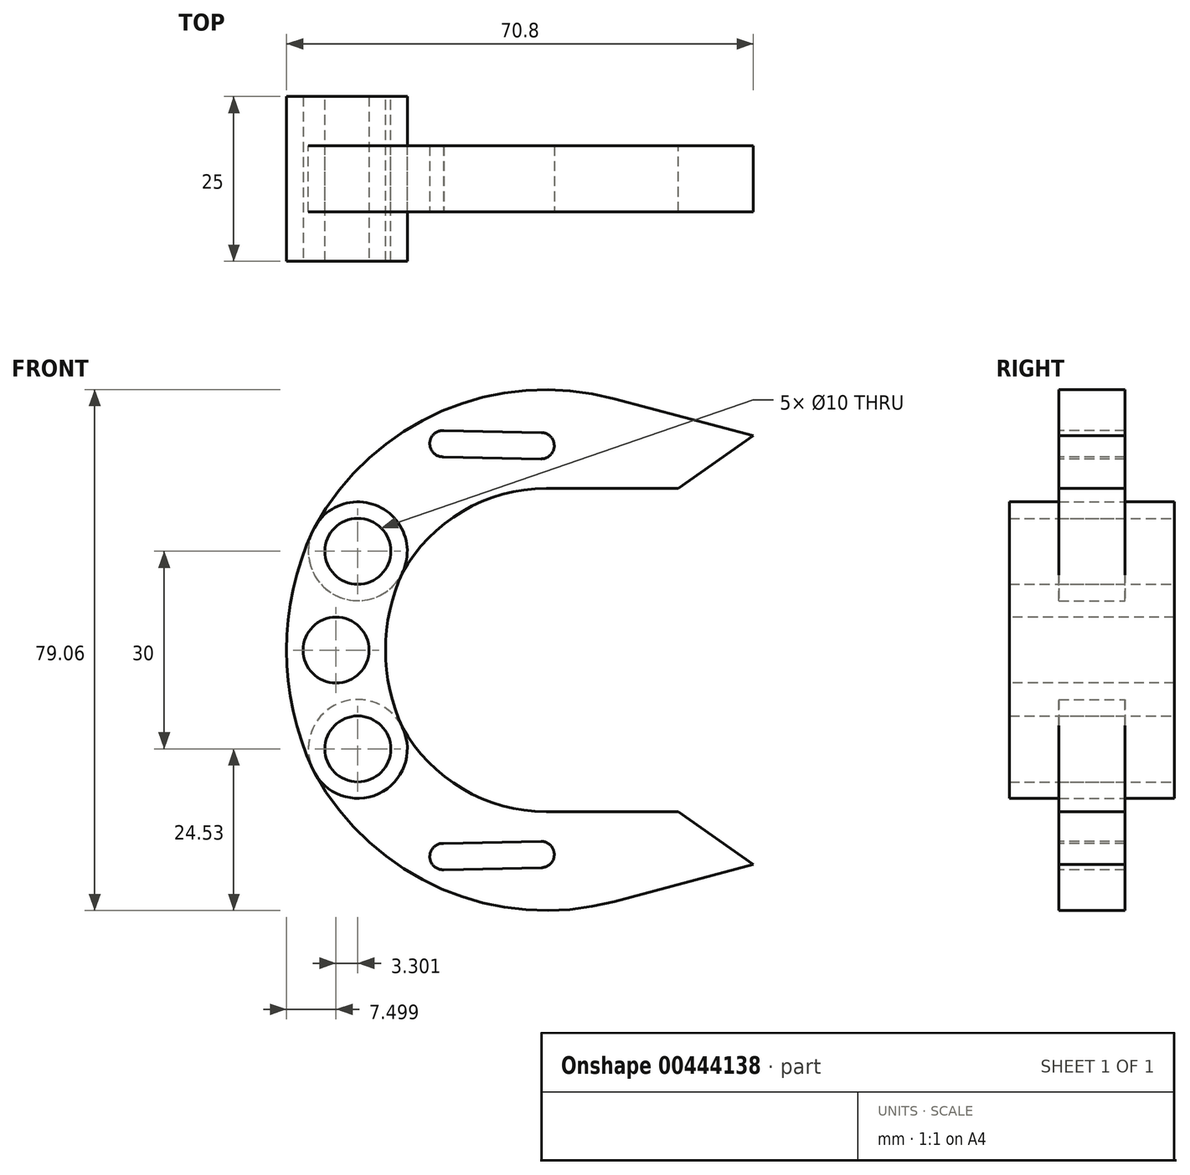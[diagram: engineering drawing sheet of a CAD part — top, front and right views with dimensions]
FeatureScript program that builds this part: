
annotation { "Feature Type Name" : "Feature", "Feature Type Description" : "" }
export const myFeature = defineFeature(function(context is Context, id is Id, definition is map)
    precondition{}
    {
        {
            var Q0;
            Q0=qCreatedBy(makeId("Front.planeOp"),FACE);
            var sketch = newSketch(context, id + "F0", { "sketchPlane" : qUnion([Q0])});
            skLineSegment(sketch, "E0", {"start": v(0, 15) * mm, "end": v(0, -15) * mm, "construction": true});
            skLineSegment(sketch, "E1", {"start": v(0, 0) * mm, "end": v(80, 0) * mm, "construction": true});
            skCircle(sketch, "E2", {"center": v(0, 15) * mm, "radius": 5 * mm});
            skCircle(sketch, "E3", {"center": v(0, -15) * mm, "radius": 5 * mm});
            skArc(sketch, "E4.0", {"start": v(6.8, 11.85) * mm, "mid": v(3.15, 21.8) * mm, "end": v(-6.8, 18.15) * mm});
            skArc(sketch, "E5.0", {"start": v(-6.8, -18.15) * mm, "mid": v(3.15, -21.8) * mm, "end": v(6.8, -11.85) * mm});
            skArc(sketch, "E6", {"start": v(-6.8, 18.15) * mm, "mid": v(-10.8, 0) * mm, "end": v(-6.8, -18.15) * mm});
            skArc(sketch, "E7", {"start": v(6.8, 11.85) * mm, "mid": v(4.2, 0) * mm, "end": v(6.8, -11.85) * mm});
            skPoint(sketch, "E8.orphan", {"position": v(0, -28.59) * mm});
            skSolve(sketch);
        }
        {
            var Q0;
            Q0=qCreatedBy(makeId("Front.planeOp"),FACE);
            var sketch = newSketch(context, id + "F1", { "sketchPlane" : qUnion([Q0])});
            skCircle(sketch, "E9.0", {"center": v(0, 15) * mm, "radius": 5 * mm});
            skCircle(sketch, "E10", {"center": v(0, 15) * mm, "radius": 7.5 * mm});
            skArc(sketch, "E11", {"start": v(38.92, 38.17) * mm, "mid": v(12.76, 36.27) * mm, "end": v(-6.6, 18.57) * mm});
            skLineSegment(sketch, "E12", {"start": v(38.92, 38.17) * mm, "end": v(60, 32.53) * mm});
            skLineSegment(sketch, "E13", {"start": v(60, 32.53) * mm, "end": v(48.58, 24.53) * mm});
            skLineSegment(sketch, "E14", {"start": v(48.58, 24.53) * mm, "end": v(28.58, 24.53) * mm});
            skArc(sketch, "E15", {"start": v(28.58, 24.53) * mm, "mid": v(15.79, 21) * mm, "end": v(6.6, 11.43) * mm});
            skLineSegment(sketch, "E16", {"start": v(38.92, 38.17) * mm, "end": v(37.45, 29.8) * mm, "construction": true});
            skLineSegment(sketch, "E17", {"start": v(37.45, 29.8) * mm, "end": v(22.96, 33.68) * mm, "construction": true});
            skArc(sketch, "E18.MirrorCS", {"start": v(38.92, -38.17) * mm, "mid": v(12.76, -36.27) * mm, "end": v(-6.6, -18.57) * mm});
            skLineSegment(sketch, "E19.MirrorCS", {"start": v(38.92, -38.17) * mm, "end": v(60, -32.53) * mm});
            skLineSegment(sketch, "E20.MirrorCS", {"start": v(48.58, -24.53) * mm, "end": v(28.58, -24.53) * mm});
            skLineSegment(sketch, "E21.MirrorCS", {"start": v(60, -32.53) * mm, "end": v(48.58, -24.53) * mm});
            skArc(sketch, "E22.MirrorCS", {"start": v(28.58, -24.53) * mm, "mid": v(15.79, -21) * mm, "end": v(6.6, -11.43) * mm});
            skCircle(sketch, "E23.MirrorC", {"center": v(0, -15) * mm, "radius": 7.5 * mm});
            skCircle(sketch, "E24.MirrorC", {"center": v(0, -15) * mm, "radius": 5 * mm});
            skSolve(sketch);
        }
        {
            var Q0;
            Q0 = qSketchRegion(id + "F0", true);
            extrude(context, id + "F2", {"entities" : qUnion([Q0]), "endBound" : BoundingType.SYMMETRIC, "depth" : 25 * mm});
        }
        {
            var Q0;
            Q0 = qSketchRegion(id + "F1", true);
            extrude(context, id + "F3", {"entities" : qUnion([Q0]), "endBound" : BoundingType.SYMMETRIC, "depth" : 10 * mm});
        }
        {
            var Q0;
            Q0=makeQuery(id+"F3.opExtrude","CAP_FACE",FACE,{"disambiguationData":[OSD([sQuery(id+"F1.wireOp",EDGE,"E9.0"),sQuery(id+"F1.wireOp",EDGE,"E10"),sQuery(id+"F1.wireOp",EDGE,"E11"),sQuery(id+"F1.wireOp",EDGE,"E12"),sQuery(id+"F1.wireOp",EDGE,"E13"),sQuery(id+"F1.wireOp",EDGE,"E14"),sQuery(id+"F1.wireOp",EDGE,"E15")])],"isStart":false});
            var sketch = newSketch(context, id + "F4", { "sketchPlane" : qUnion([Q0])});
            skCircle(sketch, "E25", {"center": v(12.91, 31.34) * mm, "radius": 2 * mm});
            skCircle(sketch, "E26", {"center": v(27.8, 31.03) * mm, "radius": 2 * mm});
            skLineSegment(sketch, "E27", {"start": v(12.84, 33.33) * mm, "end": v(27.84, 33.03) * mm});
            skLineSegment(sketch, "E28", {"start": v(12.76, 29.34) * mm, "end": v(27.75, 29.03) * mm});
            skLineSegment(sketch, "E29", {"start": v(12.91, 31.34) * mm, "end": v(27.8, 31.03) * mm, "construction": true});
            skLineSegment(sketch, "E30", {"start": v(27.23, 39.5) * mm, "end": v(27.8, 31.03) * mm, "construction": true});
            skCircle(sketch, "E31.MirrorC", {"center": v(12.91, -31.34) * mm, "radius": 2 * mm});
            skCircle(sketch, "E32.MirrorC", {"center": v(27.8, -31.03) * mm, "radius": 2 * mm});
            skLineSegment(sketch, "E33.MirrorCS", {"start": v(12.76, -29.34) * mm, "end": v(27.75, -29.03) * mm});
            skLineSegment(sketch, "E34.MirrorCS", {"start": v(12.91, -31.34) * mm, "end": v(27.8, -31.03) * mm, "construction": true});
            skLineSegment(sketch, "E35.MirrorCS", {"start": v(27.23, -39.5) * mm, "end": v(27.8, -31.03) * mm, "construction": true});
            skLineSegment(sketch, "E36.MirrorCS", {"start": v(12.84, -33.33) * mm, "end": v(27.84, -33.03) * mm});
            skSolve(sketch);
        }
        {
            var Q0;
            Q0 = qSketchRegion(id + "F4", true);
            extrude(context, id + "F5", {"entities" : qUnion([Q0]), "operationType" : NewBodyOperationType.REMOVE, "endBound" : BoundingType.THROUGH_ALL, "oppositeDirection" : true, "depth" : 25 * mm});
        }
        {
            var Q0;
            Q0=makeQuery(id+"F2.opExtrude","CAP_FACE",FACE,{"disambiguationData":[OSD([sQuery(id+"F0.wireOp",EDGE,"E2"),sQuery(id+"F0.wireOp",EDGE,"E3"),sQuery(id+"F0.wireOp",EDGE,"E4.0"),sQuery(id+"F0.wireOp",EDGE,"E5.0"),sQuery(id+"F0.wireOp",EDGE,"E6"),sQuery(id+"F0.wireOp",EDGE,"E7")])],"isStart":false});
            var sketch = newSketch(context, id + "F6", { "sketchPlane" : qUnion([Q0])});
            skCircle(sketch, "E37", {"center": v(-3.3, 0) * mm, "radius": 5 * mm});
            skSolve(sketch);
        }
        {
            var Q0;
            Q0 = qSketchRegion(id + "F6", true);
            extrude(context, id + "F7", {"entities" : qUnion([Q0]), "operationType" : NewBodyOperationType.REMOVE, "endBound" : BoundingType.THROUGH_ALL, "oppositeDirection" : true, "depth" : 25 * mm});
        }
    });
